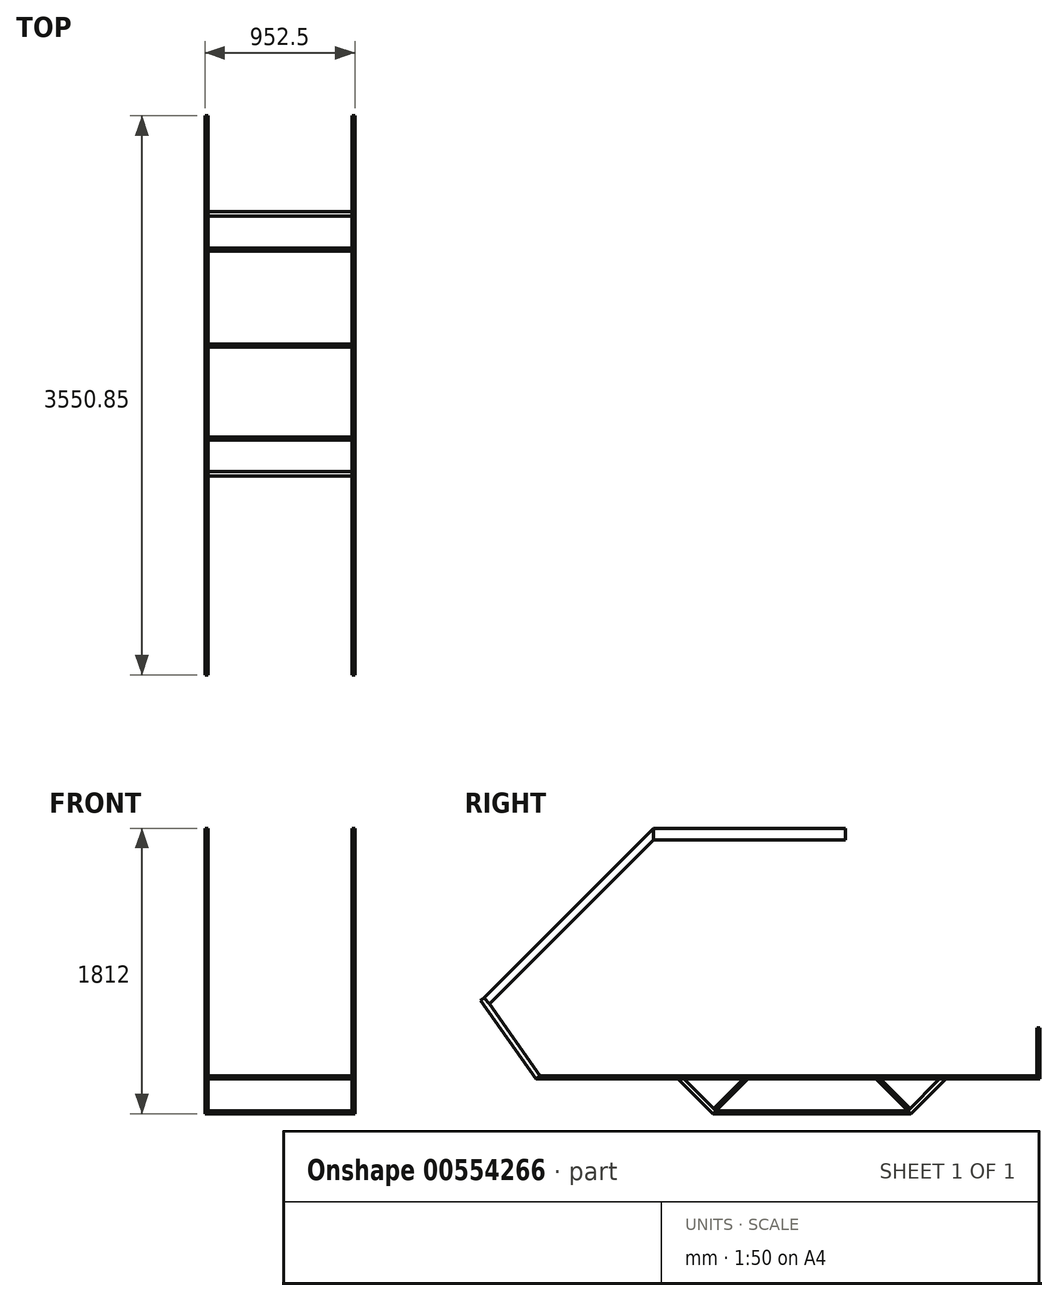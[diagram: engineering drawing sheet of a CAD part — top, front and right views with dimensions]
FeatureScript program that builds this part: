
annotation { "Feature Type Name" : "Feature", "Feature Type Description" : "" }
export const myFeature = defineFeature(function(context is Context, id is Id, definition is map)
    precondition{}
    {
        {
            var Q0;
            Q0=qCreatedBy(makeId("Front.planeOp"),FACE);
            var sketch = newSketch(context, id + "F0", { "sketchPlane" : qUnion([Q0])});
            skLineSegment(sketch, "E0", {"start": v(421.75, 0) * mm, "end": v(-492.65, 0) * mm});
            skLineSegment(sketch, "E1.bottom", {"start": v(421.75, 0) * mm, "end": v(440.8, 0) * mm});
            skLineSegment(sketch, "E1.top", {"start": v(421.75, -19.05) * mm, "end": v(440.8, -19.05) * mm});
            skLineSegment(sketch, "E1.left", {"start": v(421.75, 0) * mm, "end": v(421.75, -19.05) * mm});
            skLineSegment(sketch, "E1.right", {"start": v(440.8, 0) * mm, "end": v(440.8, -19.05) * mm});
            skLineSegment(sketch, "E2.bottom", {"start": v(-492.65, 0) * mm, "end": v(-511.7, 0) * mm});
            skLineSegment(sketch, "E2.top", {"start": v(-492.65, -19.05) * mm, "end": v(-511.7, -19.05) * mm});
            skLineSegment(sketch, "E2.left", {"start": v(-492.65, 0) * mm, "end": v(-492.65, -19.05) * mm});
            skLineSegment(sketch, "E2.right", {"start": v(-511.7, 0) * mm, "end": v(-511.7, -19.05) * mm});
            skSolve(sketch);
        }
        {
            var Q0;
            Q0=makeQuery(id+"F0.imprint","IMPRINT",FACE,{"disambiguationData":[TD([[makeQuery(id+"F0.imprint","IMPRINT",EDGE,{"derivedFrom":sQuery(id+"F0.wireOp",EDGE,"E1.bottom")}),-1.0]])]});
            var Q1;
            Q1=makeQuery(id+"F0.imprint","IMPRINT",FACE,{"disambiguationData":[TD([[makeQuery(id+"F0.imprint","IMPRINT",EDGE,{"derivedFrom":sQuery(id+"F0.wireOp",EDGE,"E2.bottom")}),1.0]])]});
            extrude(context, id + "F1", {"entities" : qUnion([Q0, Q1]), "depth" : 1219.2 * mm, "offsetDistance" : 25.4 * mm});
        }
        {
            var Q0;
            Q0=makeQuery(id+"F1.opExtrude","SWEPT_FACE",FACE,{"disambiguationData":[OSD([sQuery(id+"F0.wireOp",EDGE,"E1.left")])]});
            var sketch = newSketch(context, id + "F2", { "sketchPlane" : qUnion([Q0])});
            skLineSegment(sketch, "E3.bottom", {"start": v(0, 0) * mm, "end": v(19.05, 0) * mm});
            skLineSegment(sketch, "E3.top", {"start": v(0, -19.05) * mm, "end": v(19.05, -19.05) * mm});
            skLineSegment(sketch, "E3.left", {"start": v(0, 0) * mm, "end": v(0, -19.05) * mm});
            skLineSegment(sketch, "E3.right", {"start": v(19.05, 0) * mm, "end": v(19.05, -19.05) * mm});
            skLineSegment(sketch, "E4.bottom", {"start": v(1219.2, 0) * mm, "end": v(1200.15, 0) * mm});
            skLineSegment(sketch, "E4.top", {"start": v(1219.2, -19.05) * mm, "end": v(1200.15, -19.05) * mm});
            skLineSegment(sketch, "E4.left", {"start": v(1219.2, 0) * mm, "end": v(1219.2, -19.05) * mm});
            skLineSegment(sketch, "E4.right", {"start": v(1200.15, 0) * mm, "end": v(1200.15, -19.05) * mm});
            skLineSegment(sketch, "E5.bottom", {"start": v(609.6, 0) * mm, "end": v(628.65, 0) * mm});
            skLineSegment(sketch, "E5.top", {"start": v(609.6, -19.05) * mm, "end": v(628.65, -19.05) * mm});
            skLineSegment(sketch, "E5.left", {"start": v(609.6, 0) * mm, "end": v(609.6, -19.05) * mm});
            skLineSegment(sketch, "E5.right", {"start": v(628.65, 0) * mm, "end": v(628.65, -19.05) * mm});
            skSolve(sketch);
        }
        {
            var Q0;
            Q0 = qSketchRegion(id + "F2", true);
            extrude(context, id + "F3", {"entities" : qUnion([Q0]), "depth" : 914.4 * mm, "offsetDistance" : 25.4 * mm});
        }
        {
            var Q0;
            Q0=makeQuery(id+"F1.opExtrude","CAP_FACE",FACE,{"disambiguationData":[OSD([sQuery(id+"F0.wireOp",EDGE,"E1.bottom"),sQuery(id+"F0.wireOp",EDGE,"E1.top"),sQuery(id+"F0.wireOp",EDGE,"E1.left"),sQuery(id+"F0.wireOp",EDGE,"E1.right")])],"isStart":true});
            var Q1;
            Q1=makeQuery(id+"F1.opExtrude","CAP_FACE",FACE,{"disambiguationData":[OSD([sQuery(id+"F0.wireOp",EDGE,"E2.bottom"),sQuery(id+"F0.wireOp",EDGE,"E2.top"),sQuery(id+"F0.wireOp",EDGE,"E2.left"),sQuery(id+"F0.wireOp",EDGE,"E2.right")])],"isStart":true});
            var Q2;
            Q2=makeQuery(id+"F1.opExtrude","CAP_FACE",FACE,{"disambiguationData":[OSD([sQuery(id+"F0.wireOp",EDGE,"E1.bottom"),sQuery(id+"F0.wireOp",EDGE,"E1.top"),sQuery(id+"F0.wireOp",EDGE,"E1.left"),sQuery(id+"F0.wireOp",EDGE,"E1.right")])],"isStart":false});
            var Q3;
            Q3=makeQuery(id+"F1.opExtrude","CAP_FACE",FACE,{"disambiguationData":[OSD([sQuery(id+"F0.wireOp",EDGE,"E2.bottom"),sQuery(id+"F0.wireOp",EDGE,"E2.top"),sQuery(id+"F0.wireOp",EDGE,"E2.left"),sQuery(id+"F0.wireOp",EDGE,"E2.right")])],"isStart":false});
            extrude(context, id + "F4", {"entities" : qUnion([Q0, Q1, Q2, Q3]), "depth" : 19.05 * mm, "offsetDistance" : 25.4 * mm});
        }
        {
            var Q0;
            {var subQ0=sQuery(id+"F0.wireOp",EDGE,"E2.bottom");Q0=makeQuery(id+"F4.opExtrude","CAP_EDGE",EDGE,{"disambiguationData":[OSD([subQ0]),TDD([makeQuery(id+"F1.opExtrude","CAP_EDGE",EDGE,{"disambiguationData":[OSD([subQ0])],"isStart":true})])],"isStart":false});}
            var Q1;
            {var subQ0=sQuery(id+"F0.wireOp",EDGE,"E1.bottom");Q1=makeQuery(id+"F4.opExtrude","CAP_EDGE",EDGE,{"disambiguationData":[OSD([subQ0]),TDD([makeQuery(id+"F1.opExtrude","CAP_EDGE",EDGE,{"disambiguationData":[OSD([subQ0])],"isStart":true})])],"isStart":false});}
            chamfer(context, id + "F5", {"entities" : qUnion([Q0, Q1]), "chamferType" : ChamferType.TWO_OFFSETS, "width1" : 19.05 * mm, "oppositeDirection" : false, "width2" : 19.05 * mm, "tangentPropagation" : true});
        }
        {
            var Q0;
            Q0=makeQuery(id+"F1.opExtrude","CAP_FACE",FACE,{"disambiguationData":[OSD([sQuery(id+"F0.wireOp",EDGE,"E2.bottom"),sQuery(id+"F0.wireOp",EDGE,"E2.top"),sQuery(id+"F0.wireOp",EDGE,"E2.left"),sQuery(id+"F0.wireOp",EDGE,"E2.right")])],"isStart":false});
            var Q1;
            Q1=makeQuery(id+"F1.opExtrude","CAP_FACE",FACE,{"disambiguationData":[OSD([sQuery(id+"F0.wireOp",EDGE,"E1.bottom"),sQuery(id+"F0.wireOp",EDGE,"E1.top"),sQuery(id+"F0.wireOp",EDGE,"E1.left"),sQuery(id+"F0.wireOp",EDGE,"E1.right")])],"isStart":false});
            extrude(context, id + "F6", {"entities" : qUnion([Q0, Q1]), "depth" : 19.05 * mm, "offsetDistance" : 25.4 * mm});
        }
        {
            var Q0;
            Q0=makeQuery(id+"F6.opExtrude","CAP_EDGE",EDGE,{"disambiguationData":[OSD([sQuery(id+"F0.wireOp",EDGE,"E1.bottom")])],"isStart":false});
            var Q1;
            Q1=makeQuery(id+"F6.opExtrude","CAP_EDGE",EDGE,{"disambiguationData":[OSD([sQuery(id+"F0.wireOp",EDGE,"E2.bottom")])],"isStart":false});
            chamfer(context, id + "F7", {"entities" : qUnion([Q0, Q1]), "chamferType" : ChamferType.TWO_OFFSETS, "width1" : 19.05 * mm, "oppositeDirection" : false, "width2" : 19.05 * mm, "tangentPropagation" : true});
        }
        {
            var Q0;
            Q0=makeQuery(id+"F7.opChamfer","BLEND_FACE",FACE,{"disambiguationData":[OSD([sQuery(id+"F0.wireOp",EDGE,"E2.bottom")])]});
            var Q1;
            Q1=makeQuery(id+"F7.opChamfer","BLEND_FACE",FACE,{"disambiguationData":[OSD([sQuery(id+"F0.wireOp",EDGE,"E1.bottom")])]});
            extrude(context, id + "F8", {"entities" : qUnion([Q0, Q1]), "depth" : 304.8 * mm, "offsetDistance" : 25.4 * mm});
        }
        {
            var Q0;
            Q0=makeQuery(id+"F5.opChamfer","BLEND_FACE",FACE,{"disambiguationData":[OSD([sQuery(id+"F0.wireOp",EDGE,"E1.bottom")])]});
            var Q1;
            Q1=makeQuery(id+"F5.opChamfer","BLEND_FACE",FACE,{"disambiguationData":[OSD([sQuery(id+"F0.wireOp",EDGE,"E2.bottom")])]});
            extrude(context, id + "F9", {"entities" : qUnion([Q0, Q1]), "depth" : 304.8 * mm, "offsetDistance" : 25.4 * mm});
        }
        {
            var Q0;
            Q0=makeQuery(id+"F8.opExtrude","CAP_EDGE",EDGE,{"disambiguationData":[OSD([sQuery(id+"F0.wireOp",EDGE,"E2.bottom"),sQuery(id+"F0.wireOp",EDGE,"E2.top"),sQuery(id+"F0.wireOp",EDGE,"E2.left"),sQuery(id+"F0.wireOp",EDGE,"E2.right")])],"isStart":false});
            var Q1;
            Q1=makeQuery(id+"F8.opExtrude","CAP_EDGE",EDGE,{"disambiguationData":[OSD([sQuery(id+"F0.wireOp",EDGE,"E1.bottom"),sQuery(id+"F0.wireOp",EDGE,"E1.top"),sQuery(id+"F0.wireOp",EDGE,"E1.left"),sQuery(id+"F0.wireOp",EDGE,"E1.right")])],"isStart":false});
            chamfer(context, id + "F10", {"entities" : qUnion([Q0, Q1]), "chamferType" : ChamferType.TWO_OFFSETS, "width1" : 19.05 * mm, "oppositeDirection" : false, "width2" : 19.05 * mm, "tangentPropagation" : true});
        }
        {
            var Q0;
            Q0=makeQuery(id+"F9.opExtrude","CAP_EDGE",EDGE,{"disambiguationData":[OSD([sQuery(id+"F0.wireOp",EDGE,"E1.bottom"),sQuery(id+"F0.wireOp",EDGE,"E1.top"),sQuery(id+"F0.wireOp",EDGE,"E1.left"),sQuery(id+"F0.wireOp",EDGE,"E1.right")])],"isStart":false});
            var Q1;
            Q1=makeQuery(id+"F9.opExtrude","CAP_EDGE",EDGE,{"disambiguationData":[OSD([sQuery(id+"F0.wireOp",EDGE,"E2.bottom"),sQuery(id+"F0.wireOp",EDGE,"E2.top"),sQuery(id+"F0.wireOp",EDGE,"E2.left"),sQuery(id+"F0.wireOp",EDGE,"E2.right")])],"isStart":false});
            chamfer(context, id + "F11", {"entities" : qUnion([Q0, Q1]), "chamferType" : ChamferType.TWO_OFFSETS, "width1" : 19.05 * mm, "oppositeDirection" : false, "width2" : 19.05 * mm, "tangentPropagation" : true});
        }
        {
            var Q0;
            Q0=makeQuery(id+"F10.opChamfer","BLEND_FACE",FACE,{"disambiguationData":[OSD([sQuery(id+"F0.wireOp",EDGE,"E1.bottom"),sQuery(id+"F0.wireOp",EDGE,"E1.top"),sQuery(id+"F0.wireOp",EDGE,"E1.left"),sQuery(id+"F0.wireOp",EDGE,"E1.right")])]});
            var Q1;
            Q1=makeQuery(id+"F10.opChamfer","BLEND_FACE",FACE,{"disambiguationData":[OSD([sQuery(id+"F0.wireOp",EDGE,"E2.bottom"),sQuery(id+"F0.wireOp",EDGE,"E2.top"),sQuery(id+"F0.wireOp",EDGE,"E2.left"),sQuery(id+"F0.wireOp",EDGE,"E2.right")])]});
            var Q2;
            Q2=makeQuery(id+"F11.opChamfer","BLEND_FACE",FACE,{"disambiguationData":[OSD([sQuery(id+"F0.wireOp",EDGE,"E1.bottom"),sQuery(id+"F0.wireOp",EDGE,"E1.top"),sQuery(id+"F0.wireOp",EDGE,"E1.left"),sQuery(id+"F0.wireOp",EDGE,"E1.right")])]});
            var Q3;
            Q3=makeQuery(id+"F11.opChamfer","BLEND_FACE",FACE,{"disambiguationData":[OSD([sQuery(id+"F0.wireOp",EDGE,"E2.bottom"),sQuery(id+"F0.wireOp",EDGE,"E2.top"),sQuery(id+"F0.wireOp",EDGE,"E2.left"),sQuery(id+"F0.wireOp",EDGE,"E2.right")])]});
            extrude(context, id + "F12", {"entities" : qUnion([Q0, Q1, Q2, Q3]), "depth" : 19.05 * mm, "offsetDistance" : 25.4 * mm});
        }
        {
            var Q0;
            {var subQ0=sQuery(id+"F0.wireOp",EDGE,"E2.right");var subQ1=sQuery(id+"F0.wireOp",EDGE,"E2.left");var subQ2=sQuery(id+"F0.wireOp",EDGE,"E2.top");var subQ3=sQuery(id+"F0.wireOp",EDGE,"E2.bottom");Q0=makeQuery(id+"F12.opExtrude","SWEPT_FACE",FACE,{"disambiguationData":[OSD([subQ3,subQ2,subQ1,subQ0]),TDD([makeQuery(id+"F11.opChamfer","BLEND_EDGE",EDGE,{"blendedFrom":[makeQuery(id+"F9.opExtrude","CAP_EDGE",EDGE,{"disambiguationData":[OSD([subQ3,subQ2,subQ1,subQ0])],"isStart":false}),makeQuery(id+"F9.opExtrude","SWEPT_FACE",FACE,{"disambiguationData":[OSD([subQ3,subQ2,subQ1,subQ0])]})],"blendedInto":[makeQuery(id+"F9.opExtrude","SWEPT_FACE",FACE,{"disambiguationData":[OSD([subQ3,subQ2,subQ1,subQ0])]})]})])]});}
            var Q1;
            {var subQ0=sQuery(id+"F0.wireOp",EDGE,"E1.right");var subQ1=sQuery(id+"F0.wireOp",EDGE,"E1.left");var subQ2=sQuery(id+"F0.wireOp",EDGE,"E1.top");var subQ3=sQuery(id+"F0.wireOp",EDGE,"E1.bottom");Q1=makeQuery(id+"F12.opExtrude","SWEPT_FACE",FACE,{"disambiguationData":[OSD([subQ3,subQ2,subQ1,subQ0]),TDD([makeQuery(id+"F11.opChamfer","BLEND_EDGE",EDGE,{"blendedFrom":[makeQuery(id+"F9.opExtrude","CAP_EDGE",EDGE,{"disambiguationData":[OSD([subQ3,subQ2,subQ1,subQ0])],"isStart":false}),makeQuery(id+"F9.opExtrude","SWEPT_FACE",FACE,{"disambiguationData":[OSD([subQ3,subQ2,subQ1,subQ0])]})],"blendedInto":[makeQuery(id+"F9.opExtrude","SWEPT_FACE",FACE,{"disambiguationData":[OSD([subQ3,subQ2,subQ1,subQ0])]})]})])]});}
            extrude(context, id + "F13", {"entities" : qUnion([Q0, Q1]), "depth" : 1630.68 * mm, "offsetDistance" : 25.4 * mm});
        }
        {
            var Q0;
            Q0=makeQuery(id+"F9.opExtrude","SWEPT_FACE",FACE,{"disambiguationData":[OSD([sQuery(id+"F0.wireOp",EDGE,"E1.bottom"),sQuery(id+"F0.wireOp",EDGE,"E1.top"),sQuery(id+"F0.wireOp",EDGE,"E1.left"),sQuery(id+"F0.wireOp",EDGE,"E1.right")])]});
            var sketch = newSketch(context, id + "F14", { "sketchPlane" : qUnion([Q0])});
            skLineSegment(sketch, "E6.bottom", {"start": v(440.8, 0) * mm, "end": v(421.75, 0) * mm});
            skLineSegment(sketch, "E6.top", {"start": v(440.8, 19.05) * mm, "end": v(421.75, 19.05) * mm});
            skLineSegment(sketch, "E6.left", {"start": v(440.8, 0) * mm, "end": v(440.8, 19.05) * mm});
            skLineSegment(sketch, "E6.right", {"start": v(421.75, 0) * mm, "end": v(421.75, 19.05) * mm});
            skLineSegment(sketch, "E7.bottom", {"start": v(-511.7, 0) * mm, "end": v(-492.65, 0) * mm});
            skLineSegment(sketch, "E7.top", {"start": v(-511.7, 19.05) * mm, "end": v(-492.65, 19.05) * mm});
            skLineSegment(sketch, "E7.left", {"start": v(-511.7, 0) * mm, "end": v(-511.7, 19.05) * mm});
            skLineSegment(sketch, "E7.right", {"start": v(-492.65, 0) * mm, "end": v(-492.65, 19.05) * mm});
            skSolve(sketch);
        }
        {
            var Q0;
            Q0 = qSketchRegion(id + "F14", true);
            extrude(context, id + "F15", {"entities" : qUnion([Q0]), "depth" : 292.1 * mm, "offsetDistance" : 25.4 * mm});
        }
        {
            var Q0;
            Q0=makeQuery(id+"F8.opExtrude","SWEPT_FACE",FACE,{"disambiguationData":[OSD([sQuery(id+"F0.wireOp",EDGE,"E2.bottom"),sQuery(id+"F0.wireOp",EDGE,"E2.top"),sQuery(id+"F0.wireOp",EDGE,"E2.left"),sQuery(id+"F0.wireOp",EDGE,"E2.right")])]});
            var sketch = newSketch(context, id + "F16", { "sketchPlane" : qUnion([Q0])});
            skLineSegment(sketch, "E8.bottom", {"start": v(511.7, 862.1) * mm, "end": v(492.65, 862.1) * mm});
            skLineSegment(sketch, "E8.top", {"start": v(511.7, 881.15) * mm, "end": v(492.65, 881.15) * mm});
            skLineSegment(sketch, "E8.left", {"start": v(511.7, 862.1) * mm, "end": v(511.7, 881.15) * mm});
            skLineSegment(sketch, "E8.right", {"start": v(492.65, 862.1) * mm, "end": v(492.65, 881.15) * mm});
            skLineSegment(sketch, "E9.bottom", {"start": v(-440.8, 862.1) * mm, "end": v(-421.75, 862.1) * mm});
            skLineSegment(sketch, "E9.top", {"start": v(-440.8, 881.16) * mm, "end": v(-421.75, 881.16) * mm});
            skLineSegment(sketch, "E9.left", {"start": v(-440.8, 862.1) * mm, "end": v(-440.8, 881.16) * mm});
            skLineSegment(sketch, "E9.right", {"start": v(-421.75, 862.1) * mm, "end": v(-421.75, 881.16) * mm});
            skSolve(sketch);
        }
        {
            var Q0;
            Q0 = qSketchRegion(id + "F16", true);
            extrude(context, id + "F17", {"entities" : qUnion([Q0]), "depth" : 292.1 * mm, "offsetDistance" : 25.4 * mm});
        }
        {
            var Q0;
            {var subQ0=sQuery(id+"F0.wireOp",EDGE,"E2.left");var subQ1=sQuery(id+"F0.wireOp",EDGE,"E2.bottom");var subQ2=sQuery(id+"F0.wireOp",EDGE,"E2.right");var subQ3=sQuery(id+"F0.wireOp",EDGE,"E2.top");Q0=makeQuery(id+"F12.opExtrude","SWEPT_FACE",FACE,{"disambiguationData":[OSD([subQ1,subQ3,subQ0,subQ2]),TDD([makeQuery(id+"F10.opChamfer","BLEND_EDGE",EDGE,{"blendedFrom":[makeQuery(id+"F8.opExtrude","CAP_EDGE",EDGE,{"disambiguationData":[OSD([subQ1,subQ3,subQ0,subQ2])],"isStart":false}),makeQuery(id+"F8.opExtrude","SWEPT_FACE",FACE,{"disambiguationData":[OSD([subQ1,subQ0])]})],"blendedInto":[makeQuery(id+"F8.opExtrude","SWEPT_FACE",FACE,{"disambiguationData":[OSD([subQ1,subQ0])]})]})])]});}
            var Q1;
            {var subQ0=sQuery(id+"F0.wireOp",EDGE,"E2.left");var subQ1=sQuery(id+"F0.wireOp",EDGE,"E2.bottom");var subQ2=sQuery(id+"F0.wireOp",EDGE,"E2.right");var subQ3=sQuery(id+"F0.wireOp",EDGE,"E2.top");Q1=makeQuery(id+"F12.opExtrude","SWEPT_FACE",FACE,{"disambiguationData":[OSD([subQ1,subQ3,subQ0,subQ2]),TDD([makeQuery(id+"F11.opChamfer","BLEND_EDGE",EDGE,{"blendedFrom":[makeQuery(id+"F9.opExtrude","CAP_EDGE",EDGE,{"disambiguationData":[OSD([subQ1,subQ3,subQ0,subQ2])],"isStart":false}),makeQuery(id+"F9.opExtrude","SWEPT_FACE",FACE,{"disambiguationData":[OSD([subQ1,subQ0])]})],"blendedInto":[makeQuery(id+"F9.opExtrude","SWEPT_FACE",FACE,{"disambiguationData":[OSD([subQ1,subQ0])]})]})])]});}
            extrude(context, id + "F18", {"entities" : qUnion([Q0, Q1]), "depth" : 914.4 * mm, "offsetDistance" : 25.4 * mm});
        }
        {
            var Q0;
            {var subQ0=sQuery(id+"F0.wireOp",EDGE,"E1.bottom");var subQ1=sQuery(id+"F0.wireOp",EDGE,"E1.right");var subQ2=sQuery(id+"F0.wireOp",EDGE,"E1.left");var subQ3=sQuery(id+"F0.wireOp",EDGE,"E1.top");Q0=makeQuery(id+"F12.opExtrude","SWEPT_FACE",FACE,{"disambiguationData":[OSD([subQ0,subQ3,subQ2,subQ1]),TDD([makeQuery(id+"F11.opChamfer","BLEND_EDGE",EDGE,{"blendedFrom":[makeQuery(id+"F9.opExtrude","CAP_EDGE",EDGE,{"disambiguationData":[OSD([subQ0,subQ3,subQ2,subQ1])],"isStart":false}),makeQuery(id+"F9.opExtrude","CAP_FACE",FACE,{"disambiguationData":[OSD([subQ0])],"isStart":false})],"blendedInto":[makeQuery(id+"F9.opExtrude","CAP_FACE",FACE,{"disambiguationData":[OSD([subQ0])],"isStart":false})]})])]});}
            var Q1;
            {var subQ0=sQuery(id+"F0.wireOp",EDGE,"E2.bottom");var subQ1=sQuery(id+"F0.wireOp",EDGE,"E2.right");var subQ2=sQuery(id+"F0.wireOp",EDGE,"E2.left");var subQ3=sQuery(id+"F0.wireOp",EDGE,"E2.top");Q1=makeQuery(id+"F12.opExtrude","SWEPT_FACE",FACE,{"disambiguationData":[OSD([subQ0,subQ3,subQ2,subQ1]),TDD([makeQuery(id+"F11.opChamfer","BLEND_EDGE",EDGE,{"blendedFrom":[makeQuery(id+"F9.opExtrude","CAP_EDGE",EDGE,{"disambiguationData":[OSD([subQ0,subQ3,subQ2,subQ1])],"isStart":false}),makeQuery(id+"F9.opExtrude","CAP_FACE",FACE,{"disambiguationData":[OSD([subQ0])],"isStart":false})],"blendedInto":[makeQuery(id+"F9.opExtrude","CAP_FACE",FACE,{"disambiguationData":[OSD([subQ0])],"isStart":false})]})])]});}
            extrude(context, id + "F19", {"entities" : qUnion([Q0, Q1]), "depth" : 609.6 * mm, "offsetDistance" : 25.4 * mm});
        }
        {
            var Q0;
            {var subQ0=sQuery(id+"F0.wireOp",EDGE,"E1.bottom");var subQ1=sQuery(id+"F0.wireOp",EDGE,"E1.right");var subQ2=sQuery(id+"F0.wireOp",EDGE,"E1.left");var subQ3=sQuery(id+"F0.wireOp",EDGE,"E1.top");Q0=makeQuery(id+"F19.opExtrude","SWEPT_FACE",FACE,{"disambiguationData":[OSD([subQ0,subQ3,subQ2,subQ1]),TDD([makeQuery(id+"F12.opExtrude","CAP_EDGE",EDGE,{"disambiguationData":[OSD([subQ0,subQ3,subQ2,subQ1]),TDD([makeQuery(id+"F11.opChamfer","BLEND_EDGE",EDGE,{"blendedFrom":[makeQuery(id+"F9.opExtrude","CAP_EDGE",EDGE,{"disambiguationData":[OSD([subQ0,subQ3,subQ2,subQ1])],"isStart":false}),makeQuery(id+"F9.opExtrude","CAP_FACE",FACE,{"disambiguationData":[OSD([subQ0])],"isStart":false})],"blendedInto":[makeQuery(id+"F9.opExtrude","CAP_FACE",FACE,{"disambiguationData":[OSD([subQ0])],"isStart":false})]})])],"isStart":false})])]});}
            var sketch = newSketch(context, id + "F20", { "sketchPlane" : qUnion([Q0])});
            skLineSegment(sketch, "E10.bottom", {"start": v(-511.7, 1143.4) * mm, "end": v(-492.64, 1143.4) * mm});
            skLineSegment(sketch, "E10.top", {"start": v(-511.7, 1124.34) * mm, "end": v(-492.64, 1124.34) * mm});
            skLineSegment(sketch, "E10.left", {"start": v(-511.7, 1143.4) * mm, "end": v(-511.7, 1124.34) * mm});
            skLineSegment(sketch, "E10.right", {"start": v(-492.64, 1143.4) * mm, "end": v(-492.64, 1124.34) * mm});
            skLineSegment(sketch, "E11.bottom", {"start": v(421.75, 838.6) * mm, "end": v(440.8, 838.6) * mm});
            skLineSegment(sketch, "E11.top", {"start": v(421.75, 819.55) * mm, "end": v(440.8, 819.55) * mm});
            skLineSegment(sketch, "E11.left", {"start": v(421.75, 838.6) * mm, "end": v(421.75, 819.55) * mm});
            skLineSegment(sketch, "E11.right", {"start": v(440.8, 838.6) * mm, "end": v(440.8, 819.55) * mm});
            skLineSegment(sketch, "E12.bottom", {"start": v(-511.7, 838.6) * mm, "end": v(-492.65, 838.6) * mm});
            skLineSegment(sketch, "E12.top", {"start": v(-511.7, 819.55) * mm, "end": v(-492.65, 819.55) * mm});
            skLineSegment(sketch, "E12.left", {"start": v(-511.7, 838.6) * mm, "end": v(-511.7, 819.55) * mm});
            skLineSegment(sketch, "E12.right", {"start": v(-492.65, 838.6) * mm, "end": v(-492.65, 819.55) * mm});
            skSolve(sketch);
        }
        {
            var Q0;
            Q0 = qSketchRegion(id + "F20", true);
            extrude(context, id + "F21", {"entities" : qUnion([Q0]), "depth" : 304.8 * mm, "offsetDistance" : 25.4 * mm});
        }
        {
            var Q0;
            Q0=makeQuery(id+"F21.opExtrude","SWEPT_BODY",BODY,{"disambiguationData":[OSD([sQuery(id+"F20.wireOp",EDGE,"E10.bottom"),sQuery(id+"F20.wireOp",EDGE,"E10.top"),sQuery(id+"F20.wireOp",EDGE,"E10.left"),sQuery(id+"F20.wireOp",EDGE,"E10.right")])]});
            deleteBodies(context, id + "F22", {"entities" : qUnion([Q0])});
        }
        {
            var Q0;
            {var subQ0=sQuery(id+"F0.wireOp",EDGE,"E1.bottom");var subQ1=sQuery(id+"F0.wireOp",EDGE,"E1.right");var subQ2=sQuery(id+"F0.wireOp",EDGE,"E1.left");var subQ3=sQuery(id+"F0.wireOp",EDGE,"E1.top");Q0=makeQuery(id+"F12.opExtrude","SWEPT_FACE",FACE,{"disambiguationData":[OSD([subQ0,subQ3,subQ2,subQ1]),TDD([makeQuery(id+"F10.opChamfer","BLEND_EDGE",EDGE,{"blendedFrom":[makeQuery(id+"F8.opExtrude","CAP_EDGE",EDGE,{"disambiguationData":[OSD([subQ0,subQ3,subQ2,subQ1])],"isStart":false}),makeQuery(id+"F8.opExtrude","CAP_FACE",FACE,{"disambiguationData":[OSD([subQ0])],"isStart":false})],"blendedInto":[makeQuery(id+"F8.opExtrude","CAP_FACE",FACE,{"disambiguationData":[OSD([subQ0])],"isStart":false})]})])]});}
            var Q1;
            {var subQ0=sQuery(id+"F0.wireOp",EDGE,"E2.bottom");var subQ1=sQuery(id+"F0.wireOp",EDGE,"E2.right");var subQ2=sQuery(id+"F0.wireOp",EDGE,"E2.left");var subQ3=sQuery(id+"F0.wireOp",EDGE,"E2.top");Q1=makeQuery(id+"F12.opExtrude","SWEPT_FACE",FACE,{"disambiguationData":[OSD([subQ0,subQ3,subQ2,subQ1]),TDD([makeQuery(id+"F10.opChamfer","BLEND_EDGE",EDGE,{"blendedFrom":[makeQuery(id+"F8.opExtrude","CAP_EDGE",EDGE,{"disambiguationData":[OSD([subQ0,subQ3,subQ2,subQ1])],"isStart":false}),makeQuery(id+"F8.opExtrude","CAP_FACE",FACE,{"disambiguationData":[OSD([subQ0])],"isStart":false})],"blendedInto":[makeQuery(id+"F8.opExtrude","CAP_FACE",FACE,{"disambiguationData":[OSD([subQ0])],"isStart":false})]})])]});}
            extrude(context, id + "F23", {"entities" : qUnion([Q0, Q1]), "depth" : 914.4 * mm, "offsetDistance" : 25.4 * mm});
        }
        {
            var Q0;
            {var subQ0=sQuery(id+"F0.wireOp",EDGE,"E2.bottom");var subQ1=sQuery(id+"F0.wireOp",EDGE,"E2.right");var subQ2=sQuery(id+"F0.wireOp",EDGE,"E2.left");var subQ3=sQuery(id+"F0.wireOp",EDGE,"E2.top");Q0=makeQuery(id+"F23.opExtrude","CAP_EDGE",EDGE,{"disambiguationData":[OSD([subQ0,subQ3,subQ2,subQ1]),TDD([makeQuery(id+"F12.opExtrude","CAP_EDGE",EDGE,{"disambiguationData":[OSD([subQ0,subQ3,subQ2,subQ1]),TDD([makeQuery(id+"F10.opChamfer","BLEND_EDGE",EDGE,{"blendedFrom":[makeQuery(id+"F8.opExtrude","CAP_EDGE",EDGE,{"disambiguationData":[OSD([subQ0,subQ3,subQ2,subQ1])],"isStart":false}),makeQuery(id+"F8.opExtrude","CAP_FACE",FACE,{"disambiguationData":[OSD([subQ0])],"isStart":false})],"blendedInto":[makeQuery(id+"F8.opExtrude","CAP_FACE",FACE,{"disambiguationData":[OSD([subQ0])],"isStart":false})]})])],"isStart":false})])],"isStart":false});}
            var Q1;
            {var subQ0=sQuery(id+"F0.wireOp",EDGE,"E1.bottom");var subQ1=sQuery(id+"F0.wireOp",EDGE,"E1.right");var subQ2=sQuery(id+"F0.wireOp",EDGE,"E1.left");var subQ3=sQuery(id+"F0.wireOp",EDGE,"E1.top");Q1=makeQuery(id+"F23.opExtrude","CAP_EDGE",EDGE,{"disambiguationData":[OSD([subQ0,subQ3,subQ2,subQ1]),TDD([makeQuery(id+"F12.opExtrude","CAP_EDGE",EDGE,{"disambiguationData":[OSD([subQ0,subQ3,subQ2,subQ1]),TDD([makeQuery(id+"F10.opChamfer","BLEND_EDGE",EDGE,{"blendedFrom":[makeQuery(id+"F8.opExtrude","CAP_EDGE",EDGE,{"disambiguationData":[OSD([subQ0,subQ3,subQ2,subQ1])],"isStart":false}),makeQuery(id+"F8.opExtrude","CAP_FACE",FACE,{"disambiguationData":[OSD([subQ0])],"isStart":false})],"blendedInto":[makeQuery(id+"F8.opExtrude","CAP_FACE",FACE,{"disambiguationData":[OSD([subQ0])],"isStart":false})]})])],"isStart":false})])],"isStart":false});}
            chamfer(context, id + "F24", {"entities" : qUnion([Q0, Q1]), "chamferType" : ChamferType.OFFSET_ANGLE, "width" : 19.05 * mm, "oppositeDirection" : false, "angle" : 55 * degree, "tangentPropagation" : true});
        }
        {
            var Q0;
            Q0=makeQuery(id+"F24.opChamfer","BLEND_FACE",FACE,{"disambiguationData":[OSD([sQuery(id+"F0.wireOp",EDGE,"E1.bottom"),sQuery(id+"F0.wireOp",EDGE,"E1.top"),sQuery(id+"F0.wireOp",EDGE,"E1.left"),sQuery(id+"F0.wireOp",EDGE,"E1.right")])]});
            var Q1;
            Q1=makeQuery(id+"F24.opChamfer","BLEND_FACE",FACE,{"disambiguationData":[OSD([sQuery(id+"F0.wireOp",EDGE,"E2.bottom"),sQuery(id+"F0.wireOp",EDGE,"E2.top"),sQuery(id+"F0.wireOp",EDGE,"E2.left"),sQuery(id+"F0.wireOp",EDGE,"E2.right")])]});
            extrude(context, id + "F25", {"entities" : qUnion([Q0, Q1]), "depth" : 609.6 * mm, "offsetDistance" : 25.4 * mm});
        }
        {
            var Q0;
            {var subQ0=sQuery(id+"F0.wireOp",EDGE,"E2.bottom");var subQ1=sQuery(id+"F0.wireOp",EDGE,"E2.right");var subQ2=sQuery(id+"F0.wireOp",EDGE,"E2.left");var subQ3=sQuery(id+"F0.wireOp",EDGE,"E2.top");var subQ4=makeQuery(id+"F12.opExtrude","CAP_EDGE",EDGE,{"disambiguationData":[OSD([subQ0,subQ3,subQ2,subQ1]),TDD([makeQuery(id+"F10.opChamfer","BLEND_EDGE",EDGE,{"blendedFrom":[makeQuery(id+"F8.opExtrude","CAP_EDGE",EDGE,{"disambiguationData":[OSD([subQ0,subQ3,subQ2,subQ1])],"isStart":false}),makeQuery(id+"F8.opExtrude","CAP_FACE",FACE,{"disambiguationData":[OSD([subQ0])],"isStart":false})],"blendedInto":[makeQuery(id+"F8.opExtrude","CAP_FACE",FACE,{"disambiguationData":[OSD([subQ0])],"isStart":false})]})])],"isStart":false});Q0=makeQuery(id+"F25.opExtrude","CAP_EDGE",EDGE,{"disambiguationData":[OSD([subQ0,subQ3,subQ2,subQ1]),TDD([makeQuery(id+"F24.opChamfer","BLEND_EDGE",EDGE,{"blendedFrom":[makeQuery(id+"F23.opExtrude","CAP_EDGE",EDGE,{"disambiguationData":[OSD([subQ0,subQ3,subQ2,subQ1]),TDD([subQ4])],"isStart":false}),makeQuery(id+"F23.opExtrude","SWEPT_FACE",FACE,{"disambiguationData":[OSD([subQ0,subQ3,subQ2,subQ1]),TDD([subQ4])]})],"blendedInto":[makeQuery(id+"F23.opExtrude","SWEPT_FACE",FACE,{"disambiguationData":[OSD([subQ0,subQ3,subQ2,subQ1]),TDD([subQ4])]})]})])],"isStart":false});}
            var Q1;
            {var subQ0=sQuery(id+"F0.wireOp",EDGE,"E1.bottom");var subQ1=sQuery(id+"F0.wireOp",EDGE,"E1.right");var subQ2=sQuery(id+"F0.wireOp",EDGE,"E1.left");var subQ3=sQuery(id+"F0.wireOp",EDGE,"E1.top");var subQ4=makeQuery(id+"F12.opExtrude","CAP_EDGE",EDGE,{"disambiguationData":[OSD([subQ0,subQ3,subQ2,subQ1]),TDD([makeQuery(id+"F10.opChamfer","BLEND_EDGE",EDGE,{"blendedFrom":[makeQuery(id+"F8.opExtrude","CAP_EDGE",EDGE,{"disambiguationData":[OSD([subQ0,subQ3,subQ2,subQ1])],"isStart":false}),makeQuery(id+"F8.opExtrude","CAP_FACE",FACE,{"disambiguationData":[OSD([subQ0])],"isStart":false})],"blendedInto":[makeQuery(id+"F8.opExtrude","CAP_FACE",FACE,{"disambiguationData":[OSD([subQ0])],"isStart":false})]})])],"isStart":false});Q1=makeQuery(id+"F25.opExtrude","CAP_EDGE",EDGE,{"disambiguationData":[OSD([subQ0,subQ3,subQ2,subQ1]),TDD([makeQuery(id+"F24.opChamfer","BLEND_EDGE",EDGE,{"blendedFrom":[makeQuery(id+"F23.opExtrude","CAP_EDGE",EDGE,{"disambiguationData":[OSD([subQ0,subQ3,subQ2,subQ1]),TDD([subQ4])],"isStart":false}),makeQuery(id+"F23.opExtrude","SWEPT_FACE",FACE,{"disambiguationData":[OSD([subQ0,subQ3,subQ2,subQ1]),TDD([subQ4])]})],"blendedInto":[makeQuery(id+"F23.opExtrude","SWEPT_FACE",FACE,{"disambiguationData":[OSD([subQ0,subQ3,subQ2,subQ1]),TDD([subQ4])]})]})])],"isStart":false});}
            chamfer(context, id + "F26", {"entities" : qUnion([Q0, Q1]), "chamferType" : ChamferType.OFFSET_ANGLE, "width" : 50.8 * mm, "oppositeDirection" : false, "angle" : 10 * degree, "tangentPropagation" : true});
        }
        {
            var Q0;
            Q0=makeQuery(id+"F26.opChamfer","BLEND_FACE",FACE,{"disambiguationData":[OSD([sQuery(id+"F0.wireOp",EDGE,"E2.bottom"),sQuery(id+"F0.wireOp",EDGE,"E2.top"),sQuery(id+"F0.wireOp",EDGE,"E2.left"),sQuery(id+"F0.wireOp",EDGE,"E2.right")])]});
            var Q1;
            Q1=makeQuery(id+"F26.opChamfer","BLEND_FACE",FACE,{"disambiguationData":[OSD([sQuery(id+"F0.wireOp",EDGE,"E1.bottom"),sQuery(id+"F0.wireOp",EDGE,"E1.top"),sQuery(id+"F0.wireOp",EDGE,"E1.left"),sQuery(id+"F0.wireOp",EDGE,"E1.right")])]});
            extrude(context, id + "F27", {"entities" : qUnion([Q0, Q1]), "depth" : 1524 * mm, "offsetDistance" : 25.4 * mm});
        }
        {
            var Q0;
            {var subQ0=sQuery(id+"F0.wireOp",EDGE,"E2.bottom");var subQ1=sQuery(id+"F0.wireOp",EDGE,"E2.right");var subQ2=sQuery(id+"F0.wireOp",EDGE,"E2.left");var subQ3=sQuery(id+"F0.wireOp",EDGE,"E2.top");var subQ4=makeQuery(id+"F12.opExtrude","CAP_EDGE",EDGE,{"disambiguationData":[OSD([subQ0,subQ3,subQ2,subQ1]),TDD([makeQuery(id+"F10.opChamfer","BLEND_EDGE",EDGE,{"blendedFrom":[makeQuery(id+"F8.opExtrude","CAP_EDGE",EDGE,{"disambiguationData":[OSD([subQ0,subQ3,subQ2,subQ1])],"isStart":false}),makeQuery(id+"F8.opExtrude","CAP_FACE",FACE,{"disambiguationData":[OSD([subQ0])],"isStart":false})],"blendedInto":[makeQuery(id+"F8.opExtrude","CAP_FACE",FACE,{"disambiguationData":[OSD([subQ0])],"isStart":false})]})])],"isStart":false});var subQ5=makeQuery(id+"F24.opChamfer","BLEND_EDGE",EDGE,{"blendedFrom":[makeQuery(id+"F23.opExtrude","CAP_EDGE",EDGE,{"disambiguationData":[OSD([subQ0,subQ3,subQ2,subQ1]),TDD([subQ4])],"isStart":false}),makeQuery(id+"F23.opExtrude","SWEPT_FACE",FACE,{"disambiguationData":[OSD([subQ0,subQ3,subQ2,subQ1]),TDD([subQ4])]})],"blendedInto":[makeQuery(id+"F23.opExtrude","SWEPT_FACE",FACE,{"disambiguationData":[OSD([subQ0,subQ3,subQ2,subQ1]),TDD([subQ4])]})]});Q0=makeQuery(id+"F27.opExtrude","CAP_EDGE",EDGE,{"disambiguationData":[OSD([subQ0,subQ3,subQ2,subQ1]),TDD([makeQuery(id+"F26.opChamfer","BLEND_EDGE",EDGE,{"blendedFrom":[makeQuery(id+"F25.opExtrude","CAP_EDGE",EDGE,{"disambiguationData":[OSD([subQ0,subQ3,subQ2,subQ1]),TDD([subQ5])],"isStart":false}),makeQuery(id+"F25.opExtrude","SWEPT_FACE",FACE,{"disambiguationData":[OSD([subQ0,subQ3,subQ2,subQ1]),TDD([subQ5])]})],"blendedInto":[makeQuery(id+"F25.opExtrude","SWEPT_FACE",FACE,{"disambiguationData":[OSD([subQ0,subQ3,subQ2,subQ1]),TDD([subQ5])]})]})])],"isStart":false});}
            var Q1;
            {var subQ0=sQuery(id+"F0.wireOp",EDGE,"E1.bottom");var subQ1=sQuery(id+"F0.wireOp",EDGE,"E1.right");var subQ2=sQuery(id+"F0.wireOp",EDGE,"E1.left");var subQ3=sQuery(id+"F0.wireOp",EDGE,"E1.top");var subQ4=makeQuery(id+"F12.opExtrude","CAP_EDGE",EDGE,{"disambiguationData":[OSD([subQ0,subQ3,subQ2,subQ1]),TDD([makeQuery(id+"F10.opChamfer","BLEND_EDGE",EDGE,{"blendedFrom":[makeQuery(id+"F8.opExtrude","CAP_EDGE",EDGE,{"disambiguationData":[OSD([subQ0,subQ3,subQ2,subQ1])],"isStart":false}),makeQuery(id+"F8.opExtrude","CAP_FACE",FACE,{"disambiguationData":[OSD([subQ0])],"isStart":false})],"blendedInto":[makeQuery(id+"F8.opExtrude","CAP_FACE",FACE,{"disambiguationData":[OSD([subQ0])],"isStart":false})]})])],"isStart":false});var subQ5=makeQuery(id+"F24.opChamfer","BLEND_EDGE",EDGE,{"blendedFrom":[makeQuery(id+"F23.opExtrude","CAP_EDGE",EDGE,{"disambiguationData":[OSD([subQ0,subQ3,subQ2,subQ1]),TDD([subQ4])],"isStart":false}),makeQuery(id+"F23.opExtrude","SWEPT_FACE",FACE,{"disambiguationData":[OSD([subQ0,subQ3,subQ2,subQ1]),TDD([subQ4])]})],"blendedInto":[makeQuery(id+"F23.opExtrude","SWEPT_FACE",FACE,{"disambiguationData":[OSD([subQ0,subQ3,subQ2,subQ1]),TDD([subQ4])]})]});Q1=makeQuery(id+"F27.opExtrude","CAP_EDGE",EDGE,{"disambiguationData":[OSD([subQ0,subQ3,subQ2,subQ1]),TDD([makeQuery(id+"F26.opChamfer","BLEND_EDGE",EDGE,{"blendedFrom":[makeQuery(id+"F25.opExtrude","CAP_EDGE",EDGE,{"disambiguationData":[OSD([subQ0,subQ3,subQ2,subQ1]),TDD([subQ5])],"isStart":false}),makeQuery(id+"F25.opExtrude","SWEPT_FACE",FACE,{"disambiguationData":[OSD([subQ0,subQ3,subQ2,subQ1]),TDD([subQ5])]})],"blendedInto":[makeQuery(id+"F25.opExtrude","SWEPT_FACE",FACE,{"disambiguationData":[OSD([subQ0,subQ3,subQ2,subQ1]),TDD([subQ5])]})]})])],"isStart":false});}
            chamfer(context, id + "F28", {"entities" : qUnion([Q0, Q1]), "chamferType" : ChamferType.OFFSET_ANGLE, "width" : 50.8 * mm, "oppositeDirection" : false, "angle" : 45 * degree, "tangentPropagation" : true});
        }
        {
            var Q0;
            Q0=makeQuery(id+"F28.opChamfer","BLEND_FACE",FACE,{"disambiguationData":[OSD([sQuery(id+"F0.wireOp",EDGE,"E2.bottom"),sQuery(id+"F0.wireOp",EDGE,"E2.top"),sQuery(id+"F0.wireOp",EDGE,"E2.left"),sQuery(id+"F0.wireOp",EDGE,"E2.right")])]});
            var Q1;
            Q1=makeQuery(id+"F28.opChamfer","BLEND_FACE",FACE,{"disambiguationData":[OSD([sQuery(id+"F0.wireOp",EDGE,"E1.bottom"),sQuery(id+"F0.wireOp",EDGE,"E1.top"),sQuery(id+"F0.wireOp",EDGE,"E1.left"),sQuery(id+"F0.wireOp",EDGE,"E1.right")])]});
            extrude(context, id + "F29", {"entities" : qUnion([Q0, Q1]), "depth" : 1219.2 * mm, "offsetDistance" : 25.4 * mm});
        }
    });
